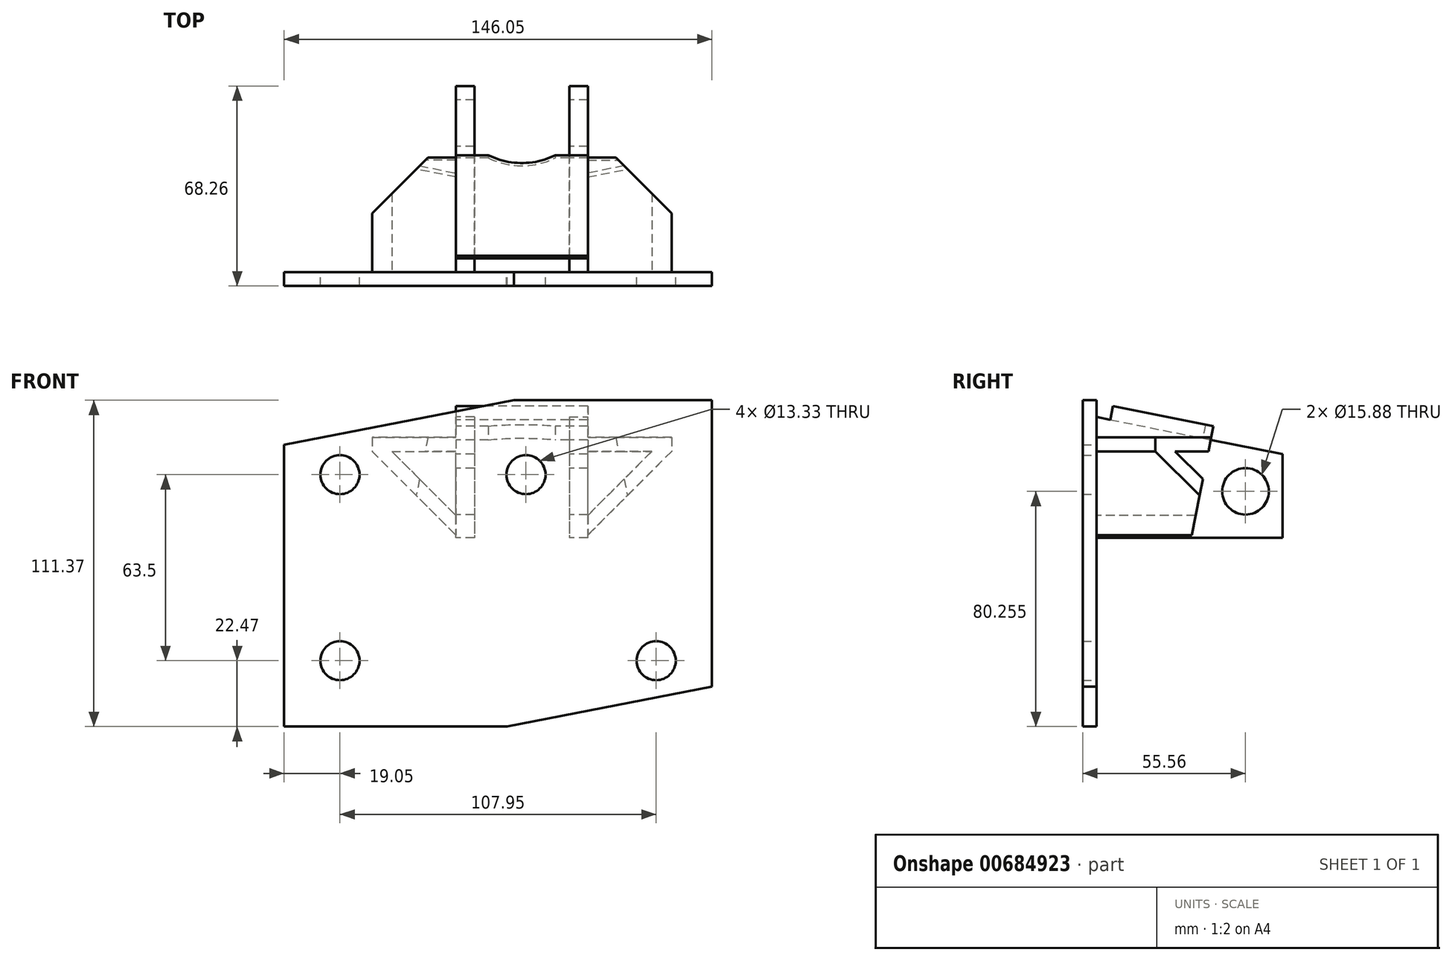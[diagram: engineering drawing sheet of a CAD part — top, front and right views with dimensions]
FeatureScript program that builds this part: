
annotation { "Feature Type Name" : "Feature", "Feature Type Description" : "" }
export const myFeature = defineFeature(function(context is Context, id is Id, definition is map)
    precondition{}
    {
        {
            var Q0;
            Q0=qCreatedBy(makeId("Front.planeOp"),FACE);
            var sketch = newSketch(context, id + "F0", { "sketchPlane" : qUnion([Q0])});
            skLineSegment(sketch, "E0.right", {"start": v(-146.05, 82.55) * mm, "end": v(-146.05, -13.58) * mm});
            skPoint(sketch, "E0.middle", {"position": v(0, -37.4) * mm});
            skCircle(sketch, "E1", {"center": v(-63.5, 72.4) * mm, "radius": 6.67 * mm});
            skCircle(sketch, "E2", {"center": v(-19.05, 8.9) * mm, "radius": 6.67 * mm});
            skPoint(sketch, "E3.startSnap0", {"position": v(-146.05, 34.49) * mm});
            skLineSegment(sketch, "E4", {"start": v(-156.26, 40.64) * mm, "end": v(11.3, 40.64) * mm, "construction": true});
            skLineSegment(sketch, "E5", {"start": v(0, 97.8) * mm, "end": v(0, 0) * mm});
            skLineSegment(sketch, "E6", {"start": v(0, 0) * mm, "end": v(-69.85, -13.58) * mm});
            skLineSegment(sketch, "E7", {"start": v(-19.05, -31.54) * mm, "end": v(-19.05, 107.9) * mm, "construction": true});
            skLineSegment(sketch, "E8", {"start": v(-69.85, -13.58) * mm, "end": v(-146.05, -13.58) * mm});
            skLineSegment(sketch, "E9", {"start": v(27.7, 8.9) * mm, "end": v(-152.82, 8.9) * mm, "construction": true});
            skLineSegment(sketch, "E10", {"start": v(-154.82, 72.39) * mm, "end": v(12.9, 72.4) * mm, "construction": true});
            skLineSegment(sketch, "E11", {"start": v(-127, 115.5) * mm, "end": v(-127, -28.35) * mm, "construction": true});
            skCircle(sketch, "E12", {"center": v(-127, 72.39) * mm, "radius": 6.67 * mm});
            skCircle(sketch, "E13", {"center": v(-127, 8.9) * mm, "radius": 6.67 * mm});
            skLineSegment(sketch, "E14", {"start": v(-146.05, 82.55) * mm, "end": v(-67.65, 97.8) * mm});
            skLineSegment(sketch, "E15", {"start": v(-67.65, 97.8) * mm, "end": v(0, 97.8) * mm});
            skSolve(sketch);
        }
        {
            var Q0;
            Q0 = qSketchRegion(id + "F0", true);
            extrude(context, id + "F1", {"entities" : qUnion([Q0]), "depth" : 4.76 * mm, "offsetDistance" : 25.4 * mm});
        }
        {
            var Q0;
            Q0=makeQuery(id+"F1.opExtrude","CAP_FACE",FACE,{"disambiguationData":[OSD([sQuery(id+"F0.wireOp",EDGE,"E0.right"),sQuery(id+"F0.wireOp",EDGE,"E1"),sQuery(id+"F0.wireOp",EDGE,"E2"),sQuery(id+"F0.wireOp",EDGE,"E5"),sQuery(id+"F0.wireOp",EDGE,"E6"),sQuery(id+"F0.wireOp",EDGE,"E8"),sQuery(id+"F0.wireOp",EDGE,"E12"),sQuery(id+"F0.wireOp",EDGE,"E13"),sQuery(id+"F0.wireOp",EDGE,"E14"),sQuery(id+"F0.wireOp",EDGE,"E15")])],"isStart":true});
            var sketch = newSketch(context, id + "F2", { "sketchPlane" : qUnion([Q0])});
            skLineSegment(sketch, "E16", {"start": v(64.91, 124.05) * mm, "end": v(64.91, -29.02) * mm, "construction": true});
            skLineSegment(sketch, "E17", {"start": v(48.72, 92.08) * mm, "end": v(48.72, 25.4) * mm});
            skLineSegment(sketch, "E18", {"start": v(48.72, 25.4) * mm, "end": v(42.37, 25.4) * mm});
            skLineSegment(sketch, "E19", {"start": v(42.37, 25.4) * mm, "end": v(42.37, 92.08) * mm});
            skLineSegment(sketch, "E20", {"start": v(48.72, 92.08) * mm, "end": v(42.37, 92.08) * mm});
            skLineSegment(sketch, "E21.MirrorCS", {"start": v(81.1, 92.08) * mm, "end": v(87.45, 92.08) * mm});
            skLineSegment(sketch, "E22.MirrorCS", {"start": v(81.1, 92.08) * mm, "end": v(81.1, 25.4) * mm});
            skLineSegment(sketch, "E23.MirrorCS", {"start": v(81.1, 25.4) * mm, "end": v(87.45, 25.4) * mm});
            skLineSegment(sketch, "E24.MirrorCS", {"start": v(87.45, 25.4) * mm, "end": v(87.45, 92.08) * mm});
            skSolve(sketch);
        }
        {
            var Q0;
            Q0 = qSketchRegion(id + "F2", true);
            extrude(context, id + "F3", {"entities" : qUnion([Q0]), "operationType" : NewBodyOperationType.ADD, "depth" : 63.5 * mm, "offsetDistance" : 25.4 * mm});
        }
        {
            var Q0;
            Q0=makeQuery(id+"F3.opExtrude","SWEPT_FACE",FACE,{"disambiguationData":[OSD([sQuery(id+"F2.wireOp",EDGE,"E24.MirrorCS")])]});
            var sketch = newSketch(context, id + "F4", { "sketchPlane" : qUnion([Q0])});
            skLineSegment(sketch, "E25", {"start": v(0, 92.08) * mm, "end": v(-63.5, 79.38) * mm});
            skLineSegment(sketch, "E26", {"start": v(-63.5, 79.38) * mm, "end": v(-63.5, 92.08) * mm});
            skLineSegment(sketch, "E27", {"start": v(-63.5, 92.08) * mm, "end": v(0, 92.08) * mm});
            skLineSegment(sketch, "E28", {"start": v(-86.86, 66.67) * mm, "end": v(44, 66.68) * mm, "construction": true});
            skLineSegment(sketch, "E29", {"start": v(-50.8, 99.25) * mm, "end": v(-50.8, 4.45) * mm, "construction": true});
            skCircle(sketch, "E30", {"center": v(-50.8, 66.68) * mm, "radius": 7.94 * mm});
            skLineSegment(sketch, "E31", {"start": v(-63.5, 50.8) * mm, "end": v(0, 50.8) * mm});
            skLineSegment(sketch, "E32", {"start": v(0, 50.8) * mm, "end": v(0, 25.4) * mm});
            skLineSegment(sketch, "E33", {"start": v(0, 25.4) * mm, "end": v(-63.5, 25.4) * mm});
            skLineSegment(sketch, "E34", {"start": v(-63.5, 25.4) * mm, "end": v(-63.5, 50.8) * mm});
            skSolve(sketch);
        }
        {
            var Q0;
            Q0 = qSketchRegion(id + "F4", true);
            extrude(context, id + "F5", {"entities" : qUnion([Q0]), "operationType" : NewBodyOperationType.REMOVE, "endBound" : BoundingType.THROUGH_ALL, "oppositeDirection" : true, "depth" : 25.4 * mm, "offsetDistance" : 25.4 * mm});
        }
        {
            var Q0;
            {var subQ1=sQuery(id+"F2.wireOp",EDGE,"E17");Q0=makeQuery(id+"F5.boolean.opBoolean","COPY",FACE,{"disambiguationData":[TD([makeQuery(id+"F3.opExtrude","SWEPT_FACE",FACE,{"disambiguationData":[OSD([subQ1])]})])],"derivedFrom":makeQuery(id+"F5.opExtrude","SWEPT_FACE",FACE,{"disambiguationData":[OSD([sQuery(id+"F4.wireOp",EDGE,"E25")])]})});}
            var sketch = newSketch(context, id + "F6", { "sketchPlane" : qUnion([Q0])});
            skLineSegment(sketch, "E35.bottom", {"start": v(-42.37, -13.3) * mm, "end": v(-87.45, -13.3) * mm});
            skLineSegment(sketch, "E35.top", {"start": v(-42.37, 21.63) * mm, "end": v(-53.48, 21.63) * mm});
            skLineSegment(sketch, "E35.left", {"start": v(-42.37, -13.3) * mm, "end": v(-42.37, 21.63) * mm});
            skLineSegment(sketch, "E35.right", {"start": v(-87.45, -13.3) * mm, "end": v(-87.45, 21.63) * mm});
            skLineSegment(sketch, "E36", {"start": v(-64.91, -13.3) * mm, "end": v(-64.91, 30.86) * mm, "construction": true});
            skPoint(sketch, "E36.endSnap0", {"position": v(-64.91, -13.3) * mm});
            skArc(sketch, "E37", {"start": v(-76.34, 21.63) * mm, "mid": v(-64.91, 18.91) * mm, "end": v(-53.48, 21.63) * mm});
            skLineSegment(sketch, "E38.trimOffspring", {"start": v(-76.34, 21.63) * mm, "end": v(-87.45, 21.63) * mm});
            skSolve(sketch);
        }
        {
            var Q0;
            Q0 = qSketchRegion(id + "F6", true);
            extrude(context, id + "F7", {"entities" : qUnion([Q0]), "operationType" : NewBodyOperationType.ADD, "depth" : 4.76 * mm, "offsetDistance" : 25.4 * mm});
        }
        {
            var Q0;
            Q0=makeQuery(id+"F5.boolean.opBoolean","MERGE",FACE,{"derivedFrom":[makeQuery(id+"F1.opExtrude","CAP_FACE",FACE,{"disambiguationData":[OSD([sQuery(id+"F0.wireOp",EDGE,"E0.right"),sQuery(id+"F0.wireOp",EDGE,"E1"),sQuery(id+"F0.wireOp",EDGE,"E2"),sQuery(id+"F0.wireOp",EDGE,"E5"),sQuery(id+"F0.wireOp",EDGE,"E6"),sQuery(id+"F0.wireOp",EDGE,"E8"),sQuery(id+"F0.wireOp",EDGE,"E12"),sQuery(id+"F0.wireOp",EDGE,"E13"),sQuery(id+"F0.wireOp",EDGE,"E14"),sQuery(id+"F0.wireOp",EDGE,"E15")])],"isStart":true}),makeQuery(id+"F5.opExtrude","SWEPT_FACE",FACE,{"disambiguationData":[OSD([sQuery(id+"F4.wireOp",EDGE,"E32")])]})]});
            var sketch = newSketch(context, id + "F8", { "sketchPlane" : qUnion([Q0])});
            skLineSegment(sketch, "E39.bottom", {"start": v(13.8, 85.1) * mm, "end": v(42.37, 85.1) * mm});
            skLineSegment(sketch, "E39.top", {"start": v(13.8, 80.33) * mm, "end": v(42.37, 80.33) * mm});
            skLineSegment(sketch, "E39.left", {"start": v(13.8, 85.1) * mm, "end": v(13.8, 80.33) * mm});
            skLineSegment(sketch, "E39.right", {"start": v(42.37, 85.1) * mm, "end": v(42.37, 80.33) * mm});
            skLineSegment(sketch, "E40", {"start": v(48.72, 50.8) * mm, "end": v(81.1, 50.8) * mm, "construction": true});
            skLineSegment(sketch, "E41", {"start": v(64.91, 50.8) * mm, "end": v(64.91, 111.38) * mm, "construction": true});
            skLineSegment(sketch, "E42.MirrorCS", {"start": v(116.03, 85.1) * mm, "end": v(116.03, 80.33) * mm});
            skLineSegment(sketch, "E43.MirrorCS", {"start": v(116.03, 80.33) * mm, "end": v(87.45, 80.33) * mm});
            skLineSegment(sketch, "E44.MirrorCS", {"start": v(87.45, 85.1) * mm, "end": v(87.45, 80.33) * mm});
            skLineSegment(sketch, "E45.MirrorCS", {"start": v(116.03, 85.1) * mm, "end": v(87.45, 85.1) * mm});
            skSolve(sketch);
        }
        {
            var Q0;
            Q0 = qSketchRegion(id + "F8", true);
            var Q1;
            Q1=makeQuery(id+"F7.opExtrude","SWEPT_FACE",FACE,{"disambiguationData":[OSD([sQuery(id+"F6.wireOp",EDGE,"E35.top")])]});
            extrude(context, id + "F9", {"entities" : qUnion([Q0]), "operationType" : NewBodyOperationType.ADD, "endBound" : BoundingType.UP_TO_SURFACE, "depth" : 25.4 * mm, "endBoundEntityFace" : qUnion([Q1]), "offsetDistance" : 25.4 * mm});
        }
        {
            var Q0;
            Q0=makeQuery(id+"F5.boolean.opBoolean","MERGE",FACE,{"derivedFrom":[makeQuery(id+"F1.opExtrude","CAP_FACE",FACE,{"disambiguationData":[OSD([sQuery(id+"F0.wireOp",EDGE,"E0.right"),sQuery(id+"F0.wireOp",EDGE,"E1"),sQuery(id+"F0.wireOp",EDGE,"E2"),sQuery(id+"F0.wireOp",EDGE,"E5"),sQuery(id+"F0.wireOp",EDGE,"E6"),sQuery(id+"F0.wireOp",EDGE,"E8"),sQuery(id+"F0.wireOp",EDGE,"E12"),sQuery(id+"F0.wireOp",EDGE,"E13"),sQuery(id+"F0.wireOp",EDGE,"E14"),sQuery(id+"F0.wireOp",EDGE,"E15")])],"isStart":true}),makeQuery(id+"F5.opExtrude","SWEPT_FACE",FACE,{"disambiguationData":[OSD([sQuery(id+"F4.wireOp",EDGE,"E32")])]})]});
            var sketch = newSketch(context, id + "F10", { "sketchPlane" : qUnion([Q0])});
            skLineSegment(sketch, "E46", {"start": v(48.72, 50.8) * mm, "end": v(81.1, 50.8) * mm, "construction": true});
            skLineSegment(sketch, "E47", {"start": v(64.91, 50.8) * mm, "end": v(64.91, 116.65) * mm, "construction": true});
            skLineSegment(sketch, "E48", {"start": v(13.8, 80.33) * mm, "end": v(42.37, 51.75) * mm});
            skLineSegment(sketch, "E49", {"start": v(42.37, 51.75) * mm, "end": v(42.37, 58.49) * mm});
            skLineSegment(sketch, "E50", {"start": v(42.37, 58.49) * mm, "end": v(20.53, 80.33) * mm});
            skLineSegment(sketch, "E51", {"start": v(20.53, 80.33) * mm, "end": v(13.8, 80.33) * mm});
            skLineSegment(sketch, "E52.MirrorCS", {"start": v(109.3, 80.33) * mm, "end": v(116.03, 80.33) * mm});
            skLineSegment(sketch, "E53.MirrorCS", {"start": v(116.03, 80.33) * mm, "end": v(87.45, 51.75) * mm});
            skLineSegment(sketch, "E54.MirrorCS", {"start": v(87.45, 58.49) * mm, "end": v(109.3, 80.33) * mm});
            skLineSegment(sketch, "E55.MirrorCS", {"start": v(87.45, 51.75) * mm, "end": v(87.45, 58.49) * mm});
            skSolve(sketch);
        }
        {
            var Q0;
            Q0 = qSketchRegion(id + "F10", true);
            var Q1;
            {var subQ0=sQuery(id+"F6.wireOp",EDGE,"E35.top");Q1=makeQuery(id+"F9.boolean.opBoolean","MERGE",FACE,{"derivedFrom":[makeQuery(id+"F7.opExtrude","SWEPT_FACE",FACE,{"disambiguationData":[OSD([subQ0])]}),makeQuery(id+"F9.opExtrude","CAP_FACE",FACE,{"disambiguationData":[OSD([subQ0]),OD(0.0)],"isStart":false})]});}
            extrude(context, id + "F11", {"entities" : qUnion([Q0]), "operationType" : NewBodyOperationType.ADD, "endBound" : BoundingType.UP_TO_SURFACE, "depth" : 25.4 * mm, "endBoundEntityFace" : qUnion([Q1]), "offsetDistance" : 25.4 * mm});
        }
        {
            var Q0;
            Q0=makeQuery(id+"F9.opExtrude","SWEPT_FACE",FACE,{"disambiguationData":[OSD([sQuery(id+"F8.wireOp",EDGE,"E39.bottom")])]});
            var sketch = newSketch(context, id + "F12", { "sketchPlane" : qUnion([Q0])});
            skLineSegment(sketch, "E56", {"start": v(-42.37, 63.5) * mm, "end": v(-87.45, 63.5) * mm, "construction": true});
            skLineSegment(sketch, "E57", {"start": v(-64.91, 63.5) * mm, "end": v(-64.91, 22.61) * mm, "construction": true});
            skLineSegment(sketch, "E58", {"start": v(-32.84, 39.08) * mm, "end": v(-13.8, 20.03) * mm});
            skLineSegment(sketch, "E59", {"start": v(-13.8, 20.03) * mm, "end": v(-13.8, 39.08) * mm});
            skLineSegment(sketch, "E60", {"start": v(-13.8, 39.08) * mm, "end": v(-32.84, 39.08) * mm});
            skLineSegment(sketch, "E61.MirrorCS", {"start": v(-96.98, 39.08) * mm, "end": v(-116.03, 20.03) * mm});
            skLineSegment(sketch, "E62.MirrorCS", {"start": v(-116.03, 20.03) * mm, "end": v(-116.03, 39.08) * mm});
            skLineSegment(sketch, "E63.MirrorCS", {"start": v(-116.03, 39.08) * mm, "end": v(-96.98, 39.08) * mm});
            skSolve(sketch);
        }
        {
            var Q0;
            Q0 = qSketchRegion(id + "F12", true);
            extrude(context, id + "F13", {"entities" : qUnion([Q0]), "operationType" : NewBodyOperationType.REMOVE, "endBound" : BoundingType.THROUGH_ALL, "oppositeDirection" : true, "depth" : 25.4 * mm, "offsetDistance" : 25.4 * mm});
        }
    });
